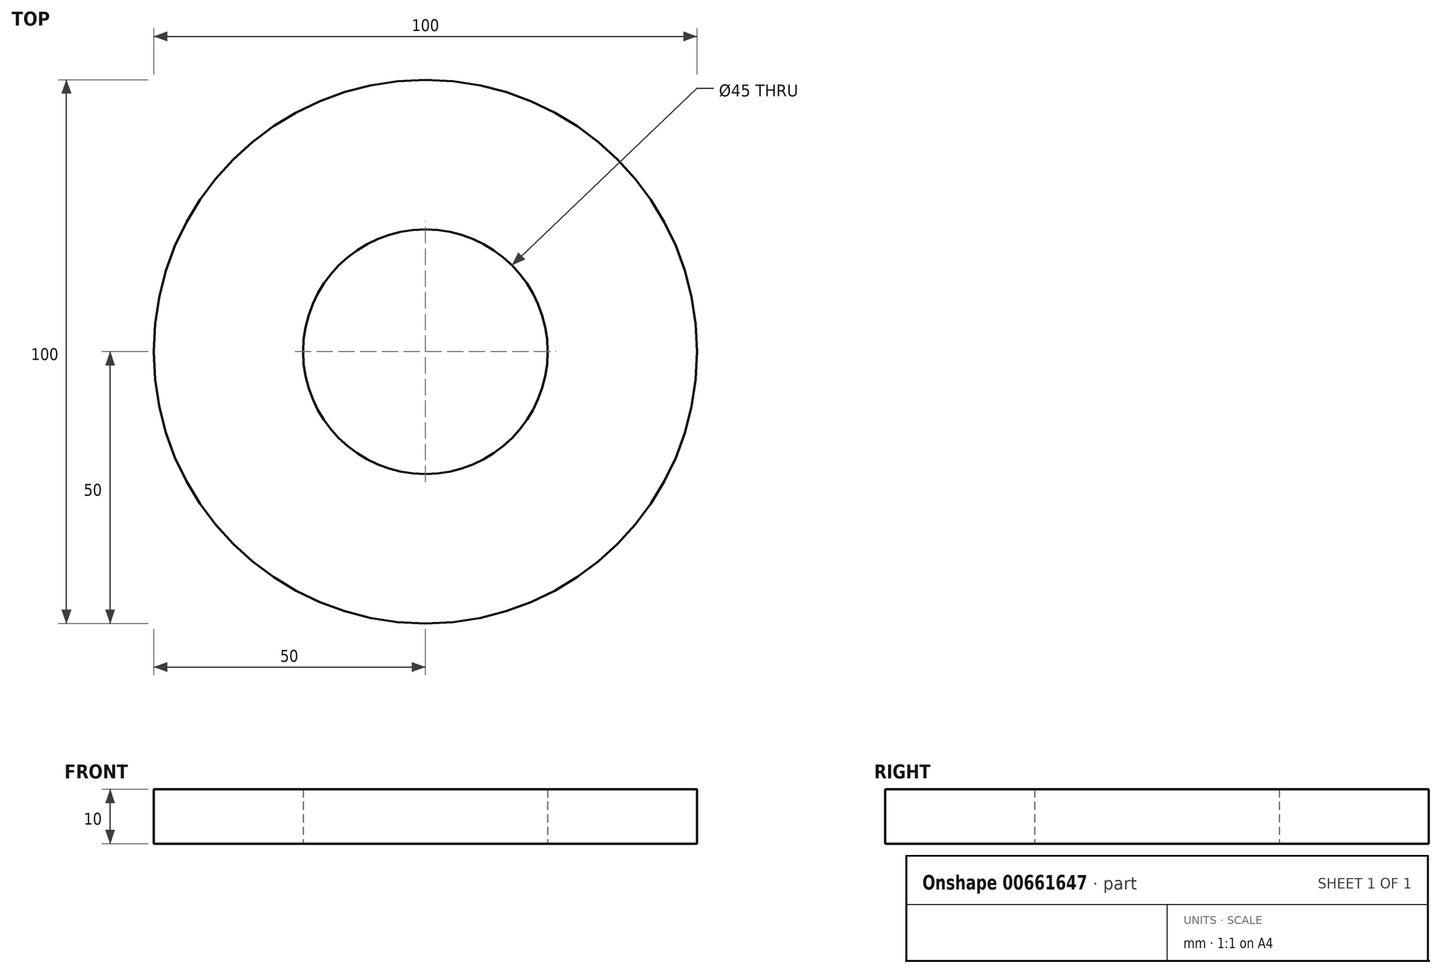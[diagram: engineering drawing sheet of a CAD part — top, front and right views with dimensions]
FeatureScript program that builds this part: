
annotation { "Feature Type Name" : "Feature", "Feature Type Description" : "" }
export const myFeature = defineFeature(function(context is Context, id is Id, definition is map)
    precondition{}
    {
        {
            var Q0;
            Q0=qCreatedBy(makeId("Top.planeOp"),FACE);
            var sketch = newSketch(context, id + "F0", { "sketchPlane" : qUnion([Q0])});
            skCircle(sketch, "E0", {"center": v(0, 0) * mm, "radius": 50 * mm});
            skCircle(sketch, "E1", {"center": v(0, 0) * mm, "radius": 22.5 * mm});
            skSolve(sketch);
        }
        {
            var Q0;
            Q0=makeQuery(id+"F0.imprint","IMPRINT",FACE,{"disambiguationData":[TD([[makeQuery(id+"F0.imprint","IMPRINT",EDGE,{"derivedFrom":sQuery(id+"F0.wireOp",EDGE,"E0")}),1.0]])]});
            extrude(context, id + "F1", {"entities" : qUnion([Q0]), "endBound" : BoundingType.SYMMETRIC, "depth" : 10 * mm, "offsetDistance" : 25 * mm});
        }
    });
